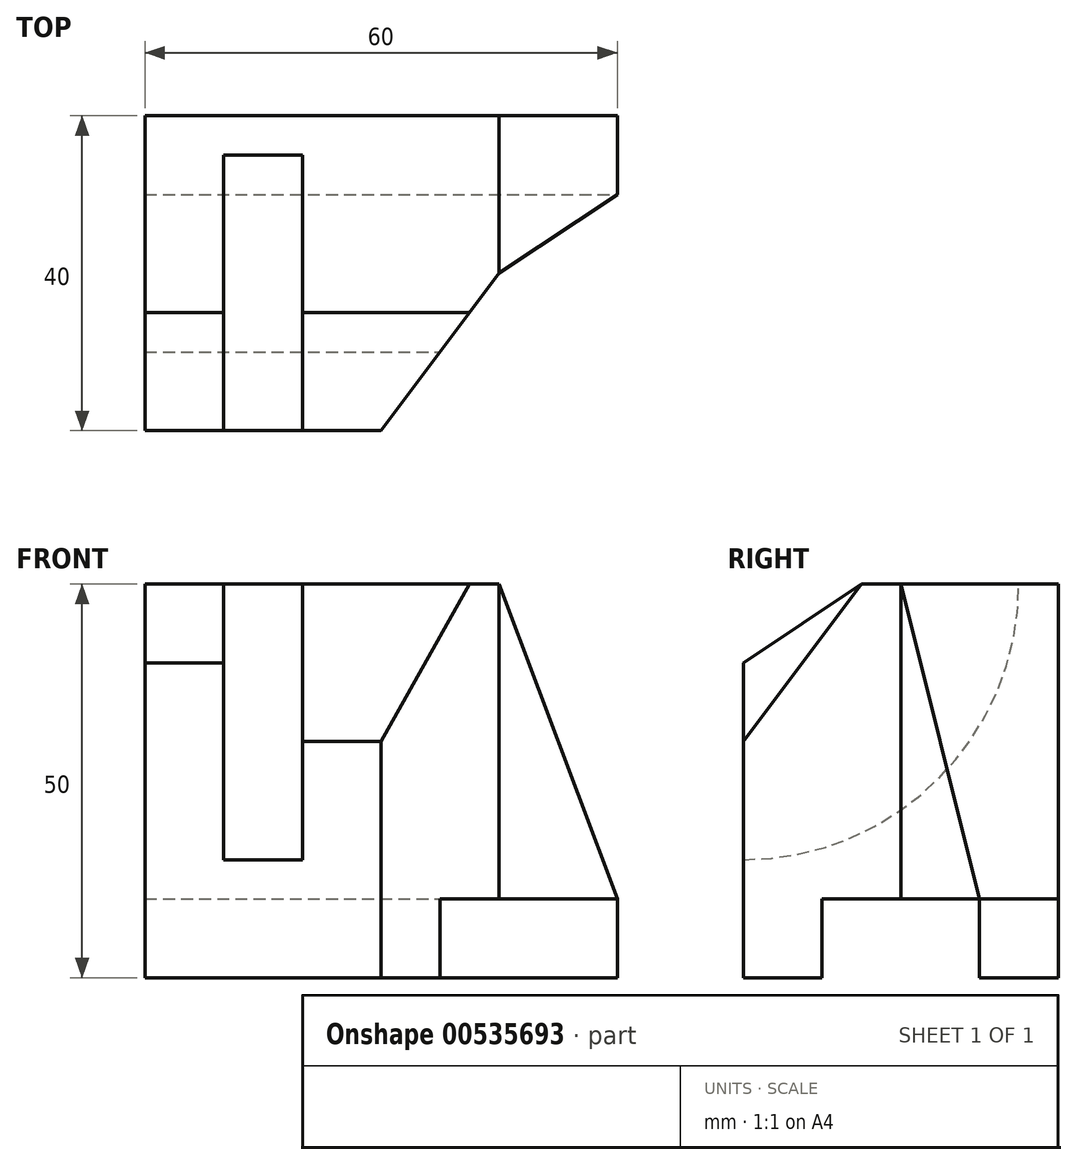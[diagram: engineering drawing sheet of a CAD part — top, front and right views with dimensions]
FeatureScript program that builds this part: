
annotation { "Feature Type Name" : "Feature", "Feature Type Description" : "" }
export const myFeature = defineFeature(function(context is Context, id is Id, definition is map)
    precondition{}
    {
        {
            var Q0;
            Q0=qCreatedBy(makeId("Top.planeOp"),FACE);
            var sketch = newSketch(context, id + "F0", { "sketchPlane" : qUnion([Q0])});
            skLineSegment(sketch, "E0.bottom", {"start": v(0, 0) * mm, "end": v(60, 0) * mm});
            skLineSegment(sketch, "E0.top", {"start": v(0, 40) * mm, "end": v(60, 40) * mm});
            skLineSegment(sketch, "E0.left", {"start": v(0, 0) * mm, "end": v(0, 40) * mm});
            skLineSegment(sketch, "E0.right", {"start": v(60, 0) * mm, "end": v(60, 40) * mm});
            skSolve(sketch);
        }
        {
            var Q0;
            Q0 = qSketchRegion(id + "F0", true);
            extrude(context, id + "F1", {"entities" : qUnion([Q0]), "depth" : 50 * mm, "offsetDistance" : 25 * mm});
        }
        {
            var Q0;
            Q0=makeQuery(id+"F1.opExtrude","SWEPT_FACE",FACE,{"disambiguationData":[OSD([sQuery(id+"F0.wireOp",EDGE,"E0.right")])]});
            var sketch = newSketch(context, id + "F2", { "sketchPlane" : qUnion([Q0])});
            skLineSegment(sketch, "E1", {"start": v(0, 0) * mm, "end": v(10, 0) * mm});
            skLineSegment(sketch, "E2", {"start": v(10, 0) * mm, "end": v(30, 0) * mm});
            skLineSegment(sketch, "E3", {"start": v(10, 0) * mm, "end": v(10, 10) * mm});
            skLineSegment(sketch, "E4", {"start": v(10, 10) * mm, "end": v(30, 10) * mm});
            skLineSegment(sketch, "E5", {"start": v(30, 10) * mm, "end": v(30, -1.5) * mm});
            skSolve(sketch);
        }
        {
            var Q0;
            Q0 = qSketchRegion(id + "F2", true);
            extrude(context, id + "F3", {"entities" : qUnion([Q0]), "operationType" : NewBodyOperationType.REMOVE, "endBound" : BoundingType.THROUGH_ALL, "oppositeDirection" : true, "depth" : 25 * mm, "offsetDistance" : 25 * mm});
        }
        {
            var Q0;
            Q0=makeQuery(id+"F1.opExtrude","SWEPT_FACE",FACE,{"disambiguationData":[OSD([sQuery(id+"F0.wireOp",EDGE,"E0.left")])]});
            cPlane(context, id + "F4", {"entities" : qUnion([Q0]), "cplaneType" : CPlaneType.OFFSET, "offset" : 20 * mm, "oppositeDirection" : true, "width" : 150 * mm, "height" : 150 * mm});
        }
        {
            var Q0;
            Q0=qCreatedBy(id+"F4.planeOp",FACE);
            var sketch = newSketch(context, id + "F5", { "sketchPlane" : qUnion([Q0])});
            skCircle(sketch, "E6", {"center": v(0, 50) * mm, "radius": 35 * mm});
            skSolve(sketch);
        }
        {
            var Q0;
            Q0 = qSketchRegion(id + "F5", true);
            extrude(context, id + "F6", {"entities" : qUnion([Q0]), "operationType" : NewBodyOperationType.REMOVE, "depth" : 10 * mm, "offsetDistance" : 25 * mm});
        }
        {
            var Q0;
            Q0=makeQuery(id+"F1.opExtrude","CAP_FACE",FACE,{"disambiguationData":[OSD([sQuery(id+"F0.wireOp",EDGE,"E0.bottom"),sQuery(id+"F0.wireOp",EDGE,"E0.top"),sQuery(id+"F0.wireOp",EDGE,"E0.left"),sQuery(id+"F0.wireOp",EDGE,"E0.right")])],"isStart":false});
            var sketch = newSketch(context, id + "F7", { "sketchPlane" : qUnion([Q0])});
            skLineSegment(sketch, "E7", {"start": v(60, 0) * mm, "end": v(40, 0) * mm});
            skLineSegment(sketch, "E8", {"start": v(0, 0) * mm, "end": v(30, 0) * mm});
            skLineSegment(sketch, "E9", {"start": v(60, 40) * mm, "end": v(45, 40) * mm});
            skLineSegment(sketch, "E10", {"start": v(45, 40) * mm, "end": v(45, 20) * mm});
            skLineSegment(sketch, "E11", {"start": v(60, 40) * mm, "end": v(60, 30) * mm});
            skLineSegment(sketch, "E12", {"start": v(30, 0) * mm, "end": v(45, 20) * mm});
            skLineSegment(sketch, "E13", {"start": v(60, 30) * mm, "end": v(45, 20) * mm});
            skLineSegment(sketch, "E14", {"start": v(60, 30) * mm, "end": v(60, 0) * mm});
            skLineSegment(sketch, "E15", {"start": v(30, 0) * mm, "end": v(60, 0) * mm});
            skSolve(sketch);
        }
        {
            var Q0;
            {var subQ0=sQuery(id+"F7.wireOp",EDGE,"E12");Q0=makeQuery(id+"F7.imprint","IMPRINT",FACE,{"disambiguationData":[TD([[makeQuery(id+"F7.imprint","IMPRINT",EDGE,{"derivedFrom":subQ0}),-1.0]])]});}
            extrude(context, id + "F8", {"entities" : qUnion([Q0]), "operationType" : NewBodyOperationType.REMOVE, "endBound" : BoundingType.THROUGH_ALL, "oppositeDirection" : true, "depth" : 25 * mm, "offsetDistance" : 25 * mm});
        }
        {
            var Q0;
            Q0=makeQuery(id+"F1.opExtrude","SWEPT_FACE",FACE,{"disambiguationData":[OSD([sQuery(id+"F0.wireOp",EDGE,"E0.left")])]});
            var sketch = newSketch(context, id + "F9", { "sketchPlane" : qUnion([Q0])});
            skLineSegment(sketch, "E16", {"start": v(0, 50) * mm, "end": v(0, 40) * mm});
            skLineSegment(sketch, "E17", {"start": v(0, 50) * mm, "end": v(-15, 50) * mm});
            skLineSegment(sketch, "E18", {"start": v(-15, 50) * mm, "end": v(0, 40) * mm});
            skSolve(sketch);
        }
        {
            var Q0;
            Q0 = qSketchRegion(id + "F9", true);
            extrude(context, id + "F10", {"entities" : qUnion([Q0]), "operationType" : NewBodyOperationType.REMOVE, "endBound" : BoundingType.UP_TO_NEXT, "oppositeDirection" : true, "depth" : 25 * mm, "offsetDistance" : 25 * mm});
        }
        {
            var Q0;
            Q0=qCreatedBy(id+"F4.planeOp",FACE);
            var sketch = newSketch(context, id + "F11", { "sketchPlane" : qUnion([Q0])});
            skLineSegment(sketch, "E19", {"start": v(0, 0) * mm, "end": v(0, 30) * mm});
            skLineSegment(sketch, "E20", {"start": v(0, 30) * mm, "end": v(0, 50) * mm});
            skLineSegment(sketch, "E21", {"start": v(0, 50) * mm, "end": v(-15, 50) * mm});
            skLineSegment(sketch, "E22", {"start": v(-15, 50) * mm, "end": v(0, 30) * mm});
            skSolve(sketch);
        }
        {
            var Q0;
            Q0 = qSketchRegion(id + "F11", true);
            extrude(context, id + "F12", {"entities" : qUnion([Q0]), "operationType" : NewBodyOperationType.REMOVE, "endBound" : BoundingType.THROUGH_ALL, "oppositeDirection" : true, "depth" : 25 * mm, "offsetDistance" : 25 * mm});
        }
        {
            var Q0;
            Q0=makeQuery(id+"F1.opExtrude","SWEPT_FACE",FACE,{"disambiguationData":[OSD([sQuery(id+"F0.wireOp",EDGE,"E0.top")])]});
            var sketch = newSketch(context, id + "F13", { "sketchPlane" : qUnion([Q0])});
            skLineSegment(sketch, "E23", {"start": v(-60, 50) * mm, "end": v(-45, 50) * mm});
            skLineSegment(sketch, "E24", {"start": v(-60, 0) * mm, "end": v(-60, 10) * mm});
            skLineSegment(sketch, "E25", {"start": v(-45, 50) * mm, "end": v(-60, 10) * mm});
            skLineSegment(sketch, "E26", {"start": v(-60, 50) * mm, "end": v(-60, 10) * mm});
            skSolve(sketch);
        }
        {
            var Q0;
            Q0 = qSketchRegion(id + "F13", true);
            extrude(context, id + "F14", {"entities" : qUnion([Q0]), "operationType" : NewBodyOperationType.REMOVE, "endBound" : BoundingType.THROUGH_ALL, "oppositeDirection" : true, "depth" : 25 * mm, "offsetDistance" : 25 * mm});
        }
    });
